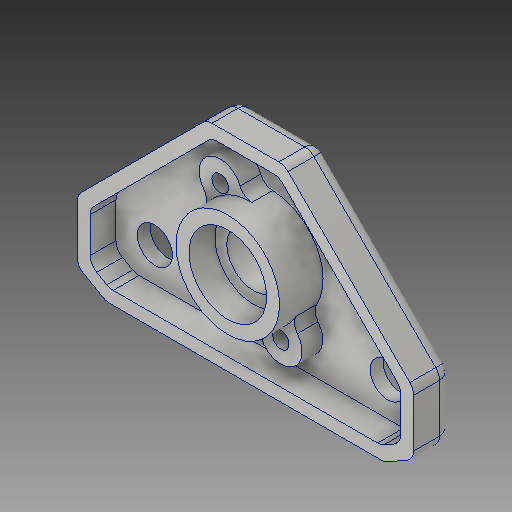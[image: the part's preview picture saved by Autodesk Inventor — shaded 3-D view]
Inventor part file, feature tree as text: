
AUTODESK INVENTOR PART (.ipt)
format: ipt  version: 2017 (Build 210142000, 142)  size: 210,432 bytes
history: native  units: in
note: dims shown in document units (in); Inventor stores cm internally (conversion verified against a paired STEP export)
features: fillet x1
ambient origin geometry x8: Origin, YZ Plane, XZ Plane, XY Plane, X Axis, Y Axis, Z Axis, Center Point
bodies: Solid1 (feature_tree)
feature tree (1):
  fillet  "Fillet2"  [1 undecoded]
note: 1 required parameter value undecoded (feature->parameter linkage not recoverable at this tier; creation-order binding heuristic only, values carry confidence <= 0.55)
